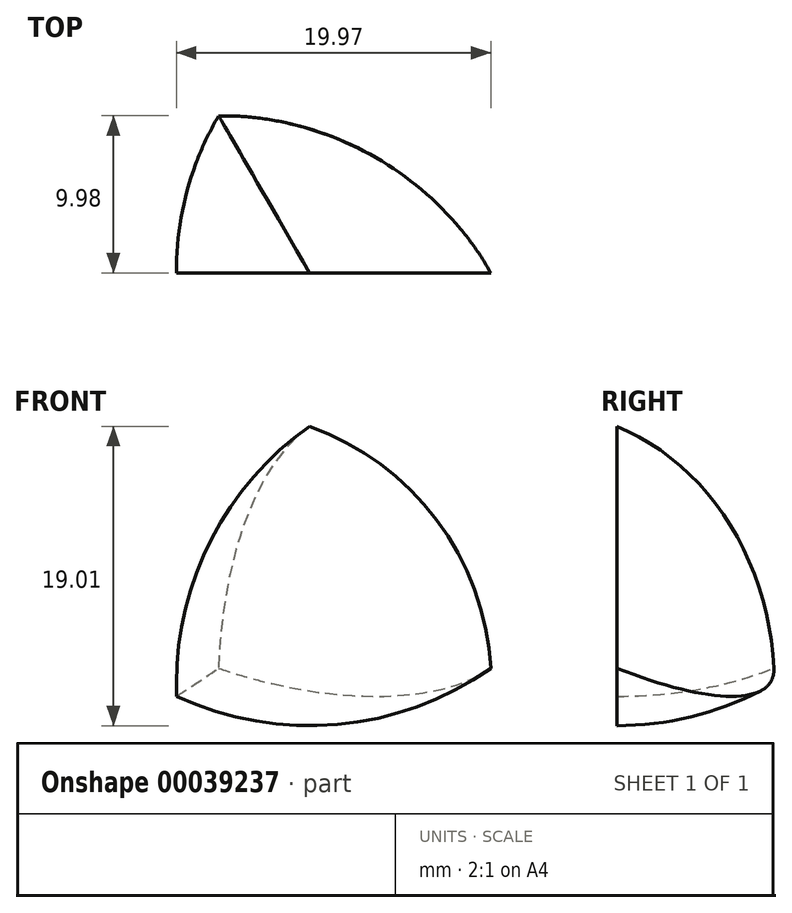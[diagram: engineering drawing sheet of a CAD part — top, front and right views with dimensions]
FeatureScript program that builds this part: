
annotation { "Feature Type Name" : "Feature", "Feature Type Description" : "" }
export const myFeature = defineFeature(function(context is Context, id is Id, definition is map)
    precondition{}
    {
        {
            var Q0;
            Q0=qCreatedBy(makeId("Top.planeOp"),FACE);
            var sketch = newSketch(context, id + "F0", { "sketchPlane" : qUnion([Q0])});
            skCircle(sketch, "E0", {"center": v(11.55, 0) * mm, "radius": 20 * mm});
            skCircle(sketch, "E1.1.0", {"center": v(-5.77, 10) * mm, "radius": 20 * mm});
            skCircle(sketch, "E1.2.0", {"center": v(-5.77, -10) * mm, "radius": 20 * mm});
            skPoint(sketch, "E1.center", {"position": v(0, 0) * mm});
            skLineSegment(sketch, "E2", {"start": v(31.55, 0) * mm, "end": v(-8.45, 0) * mm});
            skLineSegment(sketch, "E3", {"start": v(0, 0) * mm, "end": v(-5.77, -10) * mm});
            skLineSegment(sketch, "E4", {"start": v(-5.77, -10) * mm, "end": v(-15.77, -27.32) * mm});
            skLineSegment(sketch, "E5", {"start": v(0, 0) * mm, "end": v(4.23, 7.32) * mm});
            skLineSegment(sketch, "E6", {"start": v(-5.77, 10) * mm, "end": v(0, 0) * mm});
            skLineSegment(sketch, "E7", {"start": v(0, 0) * mm, "end": v(4.23, -7.32) * mm});
            skLineSegment(sketch, "E8", {"start": v(-5.77, 10) * mm, "end": v(-15.77, 27.32) * mm});
            skSolve(sketch);
        }
        {
            var Q0;
            {var subQ1=sQuery(id+"F0.wireOp",EDGE,"E2");var subQ3=sQuery(id+"F0.wireOp",EDGE,"E0");var subQ5=makeQuery(id+"F0.imprint","INTERSECT",VERTEX,{"disambiguationData":[OD(0.0)],"derivedFrom":[subQ3,subQ1]});Q0=makeQuery(id+"F0.imprint","IMPRINT",FACE,{"disambiguationData":[TD([[makeQuery(id+"F0.imprint","IMPRINT",EDGE,{"disambiguationData":[TD([[subQ5,-1.0]])],"derivedFrom":subQ3}),1.0]])]});}
            var Q1;
            {var subQ1=sQuery(id+"F0.wireOp",EDGE,"E0");var subQ4=sQuery(id+"F0.wireOp",EDGE,"E1.1.0");var subQ6=makeQuery(id+"F0.imprint","INTERSECT",VERTEX,{"derivedFrom":[subQ1,subQ4]});Q1=makeQuery(id+"F0.imprint","IMPRINT",FACE,{"disambiguationData":[TD([[makeQuery(id+"F0.imprint","IMPRINT",EDGE,{"disambiguationData":[TD([[subQ6,1.0]])],"derivedFrom":subQ4}),1.0]])]});}
            var Q2;
            {var subQ1=sQuery(id+"F0.wireOp",EDGE,"E5");Q2=makeQuery(id+"F0.imprint","IMPRINT",FACE,{"disambiguationData":[TD([[makeQuery(id+"F0.imprint","IMPRINT",EDGE,{"derivedFrom":subQ1}),1.0]])]});}
            var Q3;
            {var subQ0=sQuery(id+"F0.wireOp",EDGE,"E5");Q3=makeQuery(id+"F0.imprint","IMPRINT",FACE,{"disambiguationData":[TD([[makeQuery(id+"F0.imprint","IMPRINT",EDGE,{"derivedFrom":subQ0}),-1.0]])]});}
            var Q4;
            {var subQ0=sQuery(id+"F0.wireOp",EDGE,"E6");Q4=makeQuery(id+"F0.imprint","IMPRINT",FACE,{"disambiguationData":[TD([[makeQuery(id+"F0.imprint","IMPRINT",EDGE,{"derivedFrom":subQ0}),-1.0]])]});}
            var Q5;
            Q5=sQuery(id+"F0.wireOp",EDGE,"E2");
            revolve(context, id + "F1", {"entities" : qUnion([Q0, Q1, Q2, Q3, Q4]), "axis" : qUnion([Q5]), "revolveType" : RevolveType.FULL});
        }
        {
            var Q0;
            {var subQ1=sQuery(id+"F0.wireOp",EDGE,"E0");var subQ4=sQuery(id+"F0.wireOp",EDGE,"E1.1.0");var subQ6=makeQuery(id+"F0.imprint","INTERSECT",VERTEX,{"derivedFrom":[subQ1,subQ4]});Q0=makeQuery(id+"F0.imprint","IMPRINT",FACE,{"disambiguationData":[TD([[makeQuery(id+"F0.imprint","IMPRINT",EDGE,{"disambiguationData":[TD([[subQ6,1.0]])],"derivedFrom":subQ4}),1.0]])]});}
            var Q1;
            {var subQ0=sQuery(id+"F0.wireOp",EDGE,"E5");Q1=makeQuery(id+"F0.imprint","IMPRINT",FACE,{"disambiguationData":[TD([[makeQuery(id+"F0.imprint","IMPRINT",EDGE,{"derivedFrom":subQ0}),-1.0]])]});}
            var Q2;
            {var subQ1=sQuery(id+"F0.wireOp",EDGE,"E5");Q2=makeQuery(id+"F0.imprint","IMPRINT",FACE,{"disambiguationData":[TD([[makeQuery(id+"F0.imprint","IMPRINT",EDGE,{"derivedFrom":subQ1}),1.0]])]});}
            var Q3;
            {var subQ3=sQuery(id+"F0.wireOp",EDGE,"E7");Q3=makeQuery(id+"F0.imprint","IMPRINT",FACE,{"disambiguationData":[TD([[makeQuery(id+"F0.imprint","IMPRINT",EDGE,{"derivedFrom":subQ3}),1.0]])]});}
            var Q4;
            {var subQ0=sQuery(id+"F0.wireOp",EDGE,"E8");Q4=makeQuery(id+"F0.imprint","IMPRINT",FACE,{"disambiguationData":[TD([[makeQuery(id+"F0.imprint","IMPRINT",EDGE,{"derivedFrom":subQ0}),-1.0]])]});}
            var Q5;
            Q5=sQuery(id+"F0.wireOp",EDGE,"E8");
            revolve(context, id + "F2", {"entities" : qUnion([Q0, Q1, Q2, Q3, Q4]), "axis" : qUnion([Q5]), "revolveType" : RevolveType.FULL});
        }
        {
            var Q0;
            {var subQ3=sQuery(id+"F0.wireOp",EDGE,"E4");Q0=makeQuery(id+"F0.imprint","IMPRINT",FACE,{"disambiguationData":[TD([[makeQuery(id+"F0.imprint","IMPRINT",EDGE,{"derivedFrom":subQ3}),-1.0]])]});}
            var Q1;
            {var subQ3=sQuery(id+"F0.wireOp",EDGE,"E0");var subQ6=makeQuery(id+"F0.imprint","INTERSECT",VERTEX,{"disambiguationData":[OD(1.0)],"derivedFrom":[subQ3,sQuery(id+"F0.wireOp",EDGE,"E2")]});Q1=makeQuery(id+"F0.imprint","IMPRINT",FACE,{"disambiguationData":[TD([[makeQuery(id+"F0.imprint","IMPRINT",EDGE,{"disambiguationData":[TD([[subQ6,1.0]])],"derivedFrom":subQ3}),-1.0]])]});}
            var Q2;
            {var subQ0=sQuery(id+"F0.wireOp",EDGE,"E3");Q2=makeQuery(id+"F0.imprint","IMPRINT",FACE,{"disambiguationData":[TD([[makeQuery(id+"F0.imprint","IMPRINT",EDGE,{"derivedFrom":subQ0}),-1.0]])]});}
            var Q3;
            {var subQ0=sQuery(id+"F0.wireOp",EDGE,"E6");Q3=makeQuery(id+"F0.imprint","IMPRINT",FACE,{"disambiguationData":[TD([[makeQuery(id+"F0.imprint","IMPRINT",EDGE,{"derivedFrom":subQ0}),-1.0]])]});}
            var Q4;
            {var subQ1=sQuery(id+"F0.wireOp",EDGE,"E5");Q4=makeQuery(id+"F0.imprint","IMPRINT",FACE,{"disambiguationData":[TD([[makeQuery(id+"F0.imprint","IMPRINT",EDGE,{"derivedFrom":subQ1}),1.0]])]});}
            var Q5;
            Q5=sQuery(id+"F0.wireOp",EDGE,"E4");
            revolve(context, id + "F3", {"entities" : qUnion([Q0, Q1, Q2, Q3, Q4]), "axis" : qUnion([Q5]), "revolveType" : RevolveType.FULL});
        }
        {
            var Q0;
            Q0=qCreatedBy(makeId("Top.planeOp"),FACE);
            cPlane(context, id + "F4", {"entities" : qUnion([Q0]), "cplaneType" : CPlaneType.OFFSET, "offset" : 17.32 * mm, "width" : 150 * mm, "height" : 150 * mm});
        }
        {
            var Q0;
            Q0=qCreatedBy(id+"F4.planeOp",FACE);
            var sketch = newSketch(context, id + "F5", { "sketchPlane" : qUnion([Q0])});
            skCircle(sketch, "E9", {"center": v(0, 0) * mm, "radius": 20 * mm});
            skLineSegment(sketch, "E10", {"start": v(20, 0) * mm, "end": v(-20, 0) * mm});
            skSolve(sketch);
        }
        {
            var Q0;
            {var subQ0=sQuery(id+"F5.wireOp",EDGE,"E10");Q0=makeQuery(id+"F5.imprint","IMPRINT",FACE,{"disambiguationData":[TD([[makeQuery(id+"F5.imprint","IMPRINT",EDGE,{"derivedFrom":subQ0}),-1.0]])]});}
            var Q1;
            Q1=sQuery(id+"F5.wireOp",EDGE,"E10");
            revolve(context, id + "F6", {"entities" : qUnion([Q0]), "axis" : qUnion([Q1]), "revolveType" : RevolveType.FULL});
        }
        {
            var Q0;
            Q0=makeQuery(id+"F6.opRevolve","SWEPT_BODY",BODY,{"disambiguationData":[OSD([sQuery(id+"F5.wireOp",EDGE,"E9"),sQuery(id+"F5.wireOp",EDGE,"E10")])]});
            var Q1;
            Q1=makeQuery(id+"F1.opRevolve","SWEPT_BODY",BODY,{"disambiguationData":[OSD([sQuery(id+"F0.wireOp",EDGE,"E0"),sQuery(id+"F0.wireOp",EDGE,"E2")])]});
            var Q2;
            Q2=makeQuery(id+"F3.opRevolve","SWEPT_BODY",BODY,{"disambiguationData":[OSD([sQuery(id+"F0.wireOp",EDGE,"E1.2.0"),sQuery(id+"F0.wireOp",EDGE,"E3"),sQuery(id+"F0.wireOp",EDGE,"E4"),sQuery(id+"F0.wireOp",EDGE,"E5")])]});
            var Q3;
            Q3=makeQuery(id+"F2.opRevolve","SWEPT_BODY",BODY,{"disambiguationData":[OSD([sQuery(id+"F0.wireOp",EDGE,"E1.1.0"),sQuery(id+"F0.wireOp",EDGE,"E6"),sQuery(id+"F0.wireOp",EDGE,"E7"),sQuery(id+"F0.wireOp",EDGE,"E8")])]});
            booleanBodies(context, id + "F7", {"operationType" : BooleanOperationType.INTERSECTION, "tools" : qUnion([Q0, Q1, Q2, Q3])});
        }
        {
            var Q0;
            Q0=qCreatedBy(makeId("Front.planeOp"),FACE);
            var sketch = newSketch(context, id + "F8", { "sketchPlane" : qUnion([Q0])});
            skLineSegment(sketch, "E11.bottom", {"start": v(-24.13, 26.48) * mm, "end": v(23.54, 26.48) * mm});
            skLineSegment(sketch, "E11.top", {"start": v(-24.13, -12.28) * mm, "end": v(23.54, -12.28) * mm});
            skLineSegment(sketch, "E11.left", {"start": v(-24.13, 26.48) * mm, "end": v(-24.13, -12.28) * mm});
            skLineSegment(sketch, "E11.right", {"start": v(23.54, 26.48) * mm, "end": v(23.54, -12.28) * mm});
            skSolve(sketch);
        }
        {
            var Q0;
            Q0 = qSketchRegion(id + "F8", true);
            extrude(context, id + "F9", {"entities" : qUnion([Q0]), "depth" : 25 * mm});
        }
        {
            var Q0;
            Q0=makeQuery(id+"F9.opExtrude","SWEPT_BODY",BODY,{"disambiguationData":[OSD([sQuery(id+"F8.wireOp",EDGE,"E11.bottom"),sQuery(id+"F8.wireOp",EDGE,"E11.top"),sQuery(id+"F8.wireOp",EDGE,"E11.left"),sQuery(id+"F8.wireOp",EDGE,"E11.right")])]});
            var Q1;
            Q1=makeQuery(id+"F7.opBoolean","INTERSECT",BODY,{"derivedFrom":[makeQuery(id+"F1.opRevolve","SWEPT_BODY",BODY,{"disambiguationData":[OSD([sQuery(id+"F0.wireOp",EDGE,"E0"),sQuery(id+"F0.wireOp",EDGE,"E2")])]}),makeQuery(id+"F2.opRevolve","SWEPT_BODY",BODY,{"disambiguationData":[OSD([sQuery(id+"F0.wireOp",EDGE,"E1.1.0"),sQuery(id+"F0.wireOp",EDGE,"E6"),sQuery(id+"F0.wireOp",EDGE,"E7"),sQuery(id+"F0.wireOp",EDGE,"E8")])]}),makeQuery(id+"F3.opRevolve","SWEPT_BODY",BODY,{"disambiguationData":[OSD([sQuery(id+"F0.wireOp",EDGE,"E1.2.0"),sQuery(id+"F0.wireOp",EDGE,"E3"),sQuery(id+"F0.wireOp",EDGE,"E4"),sQuery(id+"F0.wireOp",EDGE,"E5")])]}),makeQuery(id+"F6.opRevolve","SWEPT_BODY",BODY,{"disambiguationData":[OSD([sQuery(id+"F5.wireOp",EDGE,"E9"),sQuery(id+"F5.wireOp",EDGE,"E10")])]})]});
            booleanBodies(context, id + "F10", {"operationType" : BooleanOperationType.SUBTRACTION, "tools" : qUnion([Q0]), "targets" : qUnion([Q1])});
        }
    });
